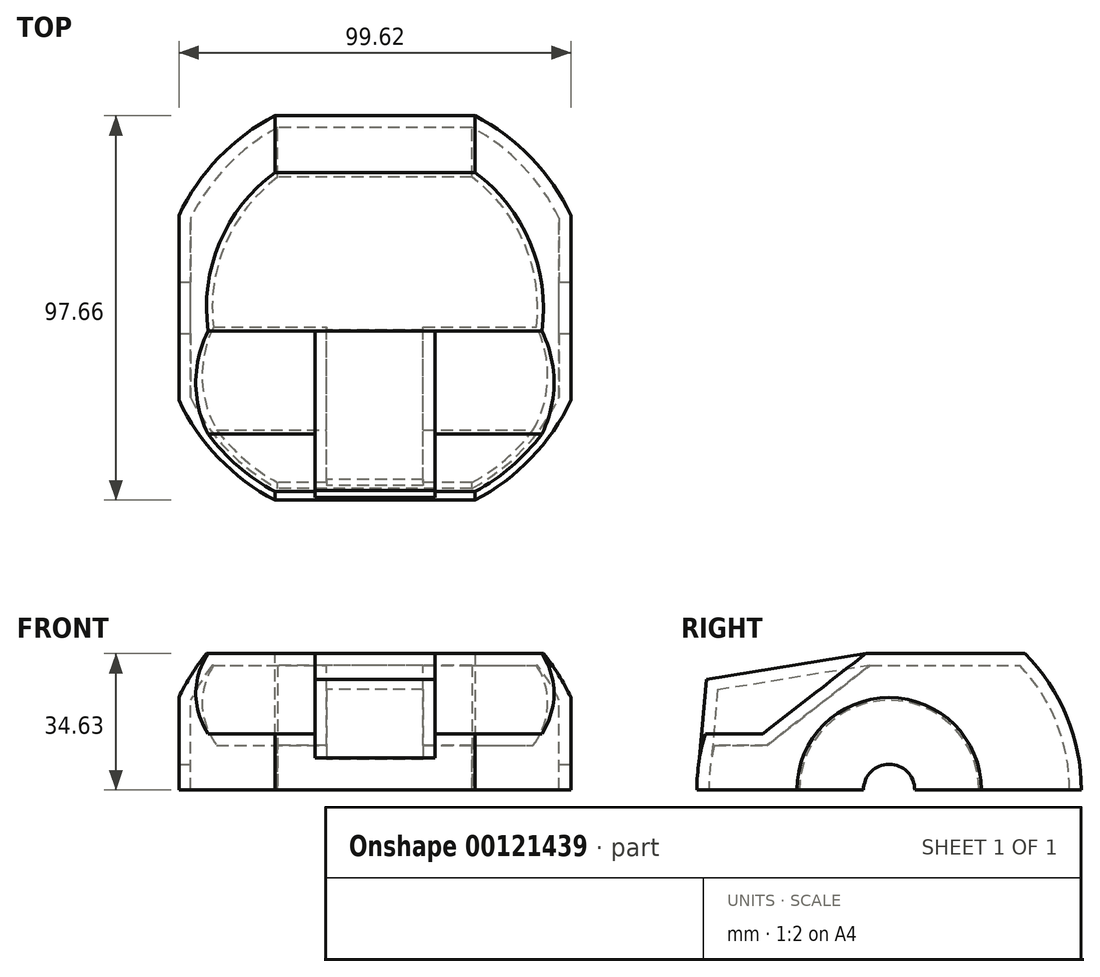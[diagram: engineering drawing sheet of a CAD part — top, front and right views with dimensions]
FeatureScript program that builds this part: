
annotation { "Feature Type Name" : "Feature", "Feature Type Description" : "" }
export const myFeature = defineFeature(function(context is Context, id is Id, definition is map)
    precondition{}
    {
        {
            var Q0;
            Q0=qCreatedBy(makeId("Top.planeOp"),FACE);
            var sketch = newSketch(context, id + "F0", { "sketchPlane" : qUnion([Q0])});
            skArc(sketch, "E0", {"start": v(0, -55.05) * mm, "mid": v(55.05, 0) * mm, "end": v(0, 55.05) * mm});
            skLineSegment(sketch, "E1", {"start": v(0, 0) * mm, "end": v(0, 55.05) * mm});
            skLineSegment(sketch, "E2", {"start": v(0, 0) * mm, "end": v(0, -55.05) * mm});
            skSolve(sketch);
        }
        {
            var Q0;
            Q0 = qSketchRegion(id + "F0", true);
            var Q1;
            Q1=sQuery(id+"F0.wireOp",EDGE,"E1");
            revolve(context, id + "F1", {"entities" : qUnion([Q0]), "axis" : qUnion([Q1]), "revolveType" : RevolveType.FULL});
        }
        {
            var Q0;
            Q0=qCreatedBy(makeId("Top.planeOp"),FACE);
            var sketch = newSketch(context, id + "F2", { "sketchPlane" : qUnion([Q0])});
            skLineSegment(sketch, "E3", {"start": v(-49.81, 26.1) * mm, "end": v(-49.81, -26.1) * mm});
            skLineSegment(sketch, "E4", {"start": v(-49.81, 26.1) * mm, "end": v(-57.5, 26.1) * mm});
            skLineSegment(sketch, "E5", {"start": v(-57.5, 26.1) * mm, "end": v(-57.5, -26.1) * mm});
            skLineSegment(sketch, "E6", {"start": v(-57.5, -26.1) * mm, "end": v(-49.81, -26.1) * mm});
            skLineSegment(sketch, "E7.MirrorCS", {"start": v(49.81, 26.1) * mm, "end": v(49.81, -26.1) * mm});
            skLineSegment(sketch, "E8.MirrorCS", {"start": v(49.81, 26.1) * mm, "end": v(57.5, 26.1) * mm});
            skLineSegment(sketch, "E9.MirrorCS", {"start": v(57.5, 26.1) * mm, "end": v(57.5, -26.1) * mm});
            skLineSegment(sketch, "E10.MirrorCS", {"start": v(57.5, -26.1) * mm, "end": v(49.81, -26.1) * mm});
            skPoint(sketch, "E11.end.orphan", {"position": v(-49.81, 0) * mm});
            skSolve(sketch);
        }
        {
            var Q0;
            Q0 = qSketchRegion(id + "F2", true);
            extrude(context, id + "F3", {"entities" : qUnion([Q0]), "operationType" : NewBodyOperationType.REMOVE, "endBound" : BoundingType.SYMMETRIC, "oppositeDirection" : true, "depth" : 50 * mm});
        }
        {
            var Q0;
            Q0=qCreatedBy(makeId("Right.planeOp"),FACE);
            var sketch = newSketch(context, id + "F4", { "sketchPlane" : qUnion([Q0])});
            skLineSegment(sketch, "E12", {"start": v(-5.9, 34.63) * mm, "end": v(42.8, 34.63) * mm});
            skLineSegment(sketch, "E13", {"start": v(-5.9, 34.63) * mm, "end": v(-32.1, 14.27) * mm});
            skLineSegment(sketch, "E14", {"start": v(-32.1, 14.27) * mm, "end": v(-53.17, 14.27) * mm});
            skArc(sketch, "E15", {"start": v(42.8, 34.63) * mm, "mid": v(-11.42, 53.85) * mm, "end": v(-53.17, 14.27) * mm});
            skPoint(sketch, "E16.orphan", {"position": v(-42.8, 34.63) * mm});
            skSolve(sketch);
        }
        {
            var Q0;
            Q0 = qSketchRegion(id + "F4", true);
            extrude(context, id + "F5", {"entities" : qUnion([Q0]), "operationType" : NewBodyOperationType.REMOVE, "endBound" : BoundingType.SYMMETRIC, "oppositeDirection" : true, "depth" : 100 * mm});
        }
        {
            var Q0;
            Q0=qCreatedBy(makeId("Right.planeOp"),FACE);
            var sketch = newSketch(context, id + "F6", { "sketchPlane" : qUnion([Q0])});
            skCircle(sketch, "E17", {"center": v(0, 0) * mm, "radius": 6.5 * mm});
            skSolve(sketch);
        }
        {
            var Q0;
            Q0 = qSketchRegion(id + "F6", true);
            extrude(context, id + "F7", {"entities" : qUnion([Q0]), "operationType" : NewBodyOperationType.REMOVE, "endBound" : BoundingType.SYMMETRIC, "oppositeDirection" : true, "depth" : 100 * mm});
        }
        {
            var Q0;
            Q0=qCreatedBy(makeId("Right.planeOp"),FACE);
            var sketch = newSketch(context, id + "F8", { "sketchPlane" : qUnion([Q0])});
            skCircle(sketch, "E18", {"center": v(0, 0) * mm, "radius": 64.9 * mm});
            skCircle(sketch, "E19", {"center": v(0, 0) * mm, "radius": 48.83 * mm});
            skSolve(sketch);
        }
        {
            var Q0;
            Q0 = qSketchRegion(id + "F8", true);
            extrude(context, id + "F9", {"entities" : qUnion([Q0]), "operationType" : NewBodyOperationType.REMOVE, "endBound" : BoundingType.SYMMETRIC, "depth" : 100 * mm});
        }
        {
            var Q0;
            Q0=qCreatedBy(makeId("Right.planeOp"),FACE);
            var sketch = newSketch(context, id + "F10", { "sketchPlane" : qUnion([Q0])});
            skLineSegment(sketch, "E20", {"start": v(-46.4, 28.07) * mm, "end": v(-5.9, 34.63) * mm});
            skLineSegment(sketch, "E21", {"start": v(-46.4, 28.07) * mm, "end": v(-48.15, 8.16) * mm});
            skLineSegment(sketch, "E22", {"start": v(-5.9, 34.63) * mm, "end": v(-34.33, 9.36) * mm});
            skLineSegment(sketch, "E23", {"start": v(-34.33, 9.36) * mm, "end": v(-48.15, 8.16) * mm});
            skSolve(sketch);
        }
        {
            var Q0;
            Q0 = qSketchRegion(id + "F10", true);
            extrude(context, id + "F11", {"entities" : qUnion([Q0]), "operationType" : NewBodyOperationType.ADD, "endBound" : BoundingType.SYMMETRIC, "depth" : 30.5 * mm});
        }
        {
            var Q0;
            Q0=qCreatedBy(makeId("Right.planeOp"),FACE);
            var sketch = newSketch(context, id + "F12", { "sketchPlane" : qUnion([Q0])});
            skLineSegment(sketch, "E24", {"start": v(-64.02, 0) * mm, "end": v(62.32, 0) * mm});
            skLineSegment(sketch, "E25", {"start": v(62.32, 0) * mm, "end": v(62.32, -54.39) * mm});
            skLineSegment(sketch, "E26", {"start": v(62.32, -54.39) * mm, "end": v(-64.02, -54.39) * mm});
            skLineSegment(sketch, "E27", {"start": v(-64.02, -54.39) * mm, "end": v(-64.02, 0) * mm});
            skSolve(sketch);
        }
        {
            var Q0;
            Q0 = qSketchRegion(id + "F12", true);
            extrude(context, id + "F13", {"entities" : qUnion([Q0]), "operationType" : NewBodyOperationType.REMOVE, "endBound" : BoundingType.SYMMETRIC, "oppositeDirection" : true, "depth" : 100 * mm});
        }
        {
            var Q0;
            Q0=makeQuery(id+"F13.boolean.opBoolean","COPY",FACE,{"disambiguationData":[OD(1.0)],"derivedFrom":makeQuery(id+"F13.opExtrude","SWEPT_FACE",FACE,{"disambiguationData":[OSD([sQuery(id+"F12.wireOp",EDGE,"E24")])]})});
            var Q1;
            Q1=makeQuery(id+"F7.boolean.opBoolean","COPY",FACE,{"derivedFrom":makeQuery(id+"F7.opExtrude","SWEPT_FACE",FACE,{"disambiguationData":[OSD([sQuery(id+"F6.wireOp",EDGE,"E17")])]})});
            var Q2;
            Q2=makeQuery(id+"F13.boolean.opBoolean","COPY",FACE,{"disambiguationData":[OD(0.0)],"derivedFrom":makeQuery(id+"F13.opExtrude","SWEPT_FACE",FACE,{"disambiguationData":[OSD([sQuery(id+"F12.wireOp",EDGE,"E24")])]})});
            shell(context, id + "F14", {"entities" : qUnion([Q0, Q1, Q2]), "thickness" : 3 * mm});
        }
    });
